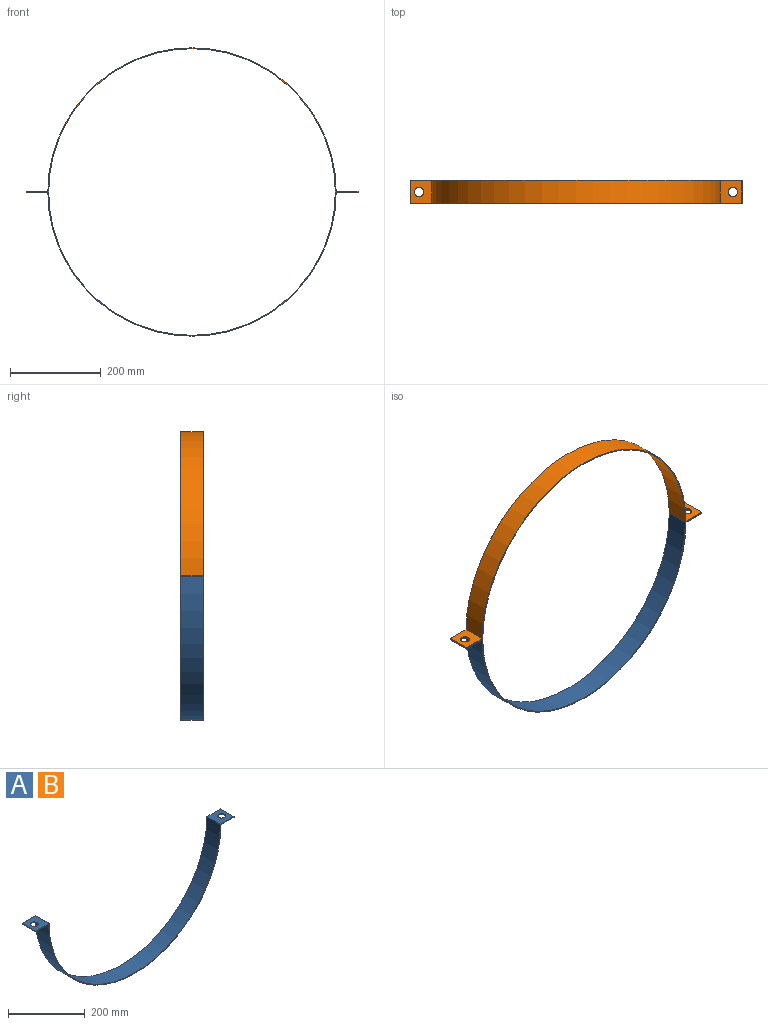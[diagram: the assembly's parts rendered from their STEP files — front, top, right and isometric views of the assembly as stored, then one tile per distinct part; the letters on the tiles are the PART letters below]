
ASSEMBLY  parts=2 mates=1
PART A: 12 faces, bbox 730x50x317 mm
  f0: plane 50x48.01mm, normal (0,0,-1), area 2086.2mm2, adj f1,f7,f8,f9,f11
  f1: plane 50x2mm, normal (1,0,0), area 100mm2, adj f0,f2,f8,f9
  f2: plane 50x50mm, normal (0,0,1), area 2185.8mm2, adj f1,f3,f8,f9,f11
  f3: cylinder r=315mm len=630mm, axis (0,1,0), area 49480.1mm2, adj f2,f4,f8,f9
  f4: plane 50x50mm, normal (0,0,1), area 2185.8mm2, adj f3,f5,f8,f9,f10
  f5: plane 50x2mm, normal (-1,0,0), area 100mm2, adj f4,f6,f8,f9
  f6: plane 50x48.01mm, normal (0,0,-1), area 2086.2mm2, adj f5,f7,f8,f9,f10
  f7: cylinder r=317mm len=633.99mm, axis (0,1,0), area 49594.2mm2, adj f0,f6,f8,f9
  f8: plane 730x317mm, normal (0,-1,0), area 2177.5mm2, adj f0,f1,f2,f3,f4,f5,f6,f7
  f9: plane 730x317mm, normal (0,1,0), area 2177.5mm2, adj f0,f1,f2,f3,f4,f5,f6,f7
  f10: cylinder r=10mm len=20mm, axis (0,0,1), area 125.7mm2, adj f4,f6
  f11: cylinder r=10mm len=20mm, axis (0,0,1), area 125.7mm2, adj f0,f2
PART B: same geometry as A
PLACE A t=(32.75,-56.73,45.05)mm fixed
PLACE B rot(axis=(0,1,0),180deg) t=(32.75,-56.73,45.05)mm
MATE fastened B.f11 <-> A.f10  axis (0,0,-1) through (-312.25,-56.73,45.05)mm
